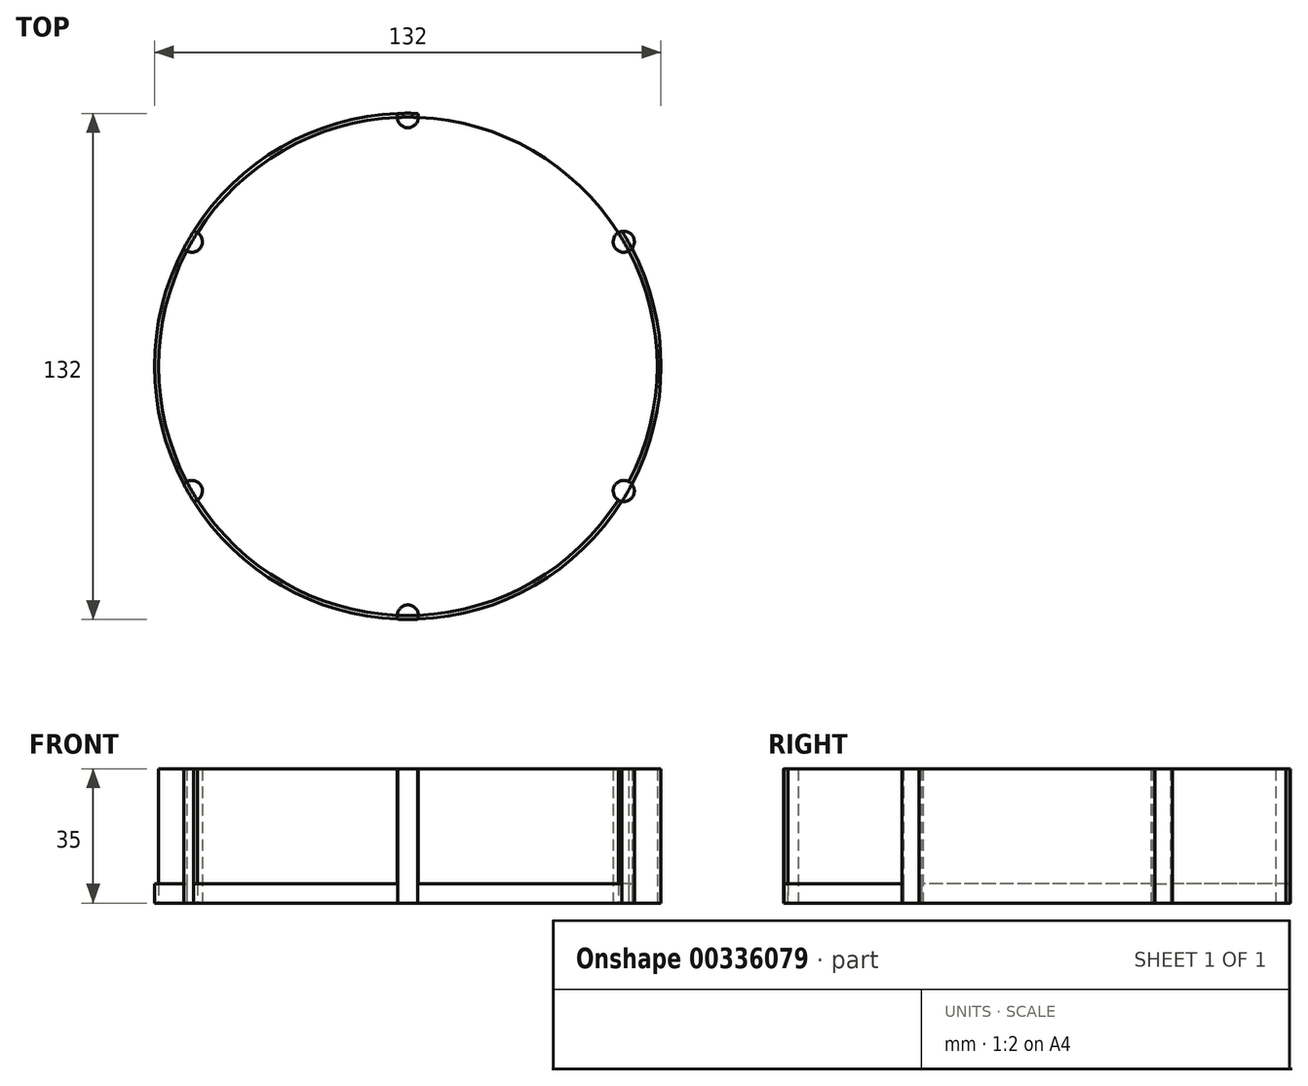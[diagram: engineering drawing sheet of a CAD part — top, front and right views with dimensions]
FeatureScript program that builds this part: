
annotation { "Feature Type Name" : "Feature", "Feature Type Description" : "" }
export const myFeature = defineFeature(function(context is Context, id is Id, definition is map)
    precondition{}
    {
        {
            var Q0;
            Q0=qCreatedBy(makeId("Top.planeOp"),FACE);
            var sketch = newSketch(context, id + "F0", { "sketchPlane" : qUnion([Q0])});
            skCircle(sketch, "E0", {"center": v(0, 0) * mm, "radius": 65 * mm});
            skCircle(sketch, "E1", {"center": v(0, 65) * mm, "radius": 2.75 * mm});
            skCircle(sketch, "E2.1.0", {"center": v(-56.3, 32.5) * mm, "radius": 2.75 * mm});
            skCircle(sketch, "E2.2.0", {"center": v(-56.3, -32.5) * mm, "radius": 2.75 * mm});
            skCircle(sketch, "E2.3.0", {"center": v(0, -65) * mm, "radius": 2.75 * mm});
            skCircle(sketch, "E2.4.0", {"center": v(56.3, -32.5) * mm, "radius": 2.75 * mm});
            skCircle(sketch, "E2.5.0", {"center": v(56.3, 32.5) * mm, "radius": 2.75 * mm});
            skCircle(sketch, "E3.0", {"center": v(0, 0) * mm, "radius": 66 * mm});
            skSolve(sketch);
        }
        {
            var Q0;
            {var subQ0=sQuery(id+"F0.wireOp",EDGE,"E2.2.0");var subQ1=sQuery(id+"F0.wireOp",EDGE,"E0");var subQ2=makeQuery(id+"F0.imprint","INTERSECT",VERTEX,{"disambiguationData":[OD(0.0)],"derivedFrom":[subQ1,subQ0]});Q0=makeQuery(id+"F0.imprint","IMPRINT",FACE,{"disambiguationData":[TD([[makeQuery(id+"F0.imprint","IMPRINT",EDGE,{"disambiguationData":[TD([[subQ2,-1.0]])],"derivedFrom":subQ1}),1.0]])]});}
            var Q1;
            {var subQ0=sQuery(id+"F0.wireOp",EDGE,"E2.2.0");var subQ1=sQuery(id+"F0.wireOp",EDGE,"E0");var subQ2=makeQuery(id+"F0.imprint","INTERSECT",VERTEX,{"disambiguationData":[OD(0.0)],"derivedFrom":[subQ1,subQ0]});Q1=makeQuery(id+"F0.imprint","IMPRINT",FACE,{"disambiguationData":[TD([[makeQuery(id+"F0.imprint","IMPRINT",EDGE,{"disambiguationData":[TD([[subQ2,-1.0]])],"derivedFrom":subQ1}),-1.0]])]});}
            var Q2;
            {var subQ0=sQuery(id+"F0.wireOp",EDGE,"E3.0");var subQ1=sQuery(id+"F0.wireOp",EDGE,"E2.2.0");var subQ2=makeQuery(id+"F0.imprint","INTERSECT",VERTEX,{"disambiguationData":[OD(0.0)],"derivedFrom":[subQ1,subQ0]});Q2=makeQuery(id+"F0.imprint","IMPRINT",FACE,{"disambiguationData":[TD([[makeQuery(id+"F0.imprint","IMPRINT",EDGE,{"disambiguationData":[TD([[subQ2,1.0]])],"derivedFrom":subQ1}),1.0]])]});}
            var Q3;
            {var subQ0=sQuery(id+"F0.wireOp",EDGE,"E2.1.0");var subQ1=sQuery(id+"F0.wireOp",EDGE,"E0");var subQ2=makeQuery(id+"F0.imprint","INTERSECT",VERTEX,{"disambiguationData":[OD(0.0)],"derivedFrom":[subQ1,subQ0]});Q3=makeQuery(id+"F0.imprint","IMPRINT",FACE,{"disambiguationData":[TD([[makeQuery(id+"F0.imprint","IMPRINT",EDGE,{"disambiguationData":[TD([[subQ2,-1.0]])],"derivedFrom":subQ1}),1.0]])]});}
            var Q4;
            {var subQ0=sQuery(id+"F0.wireOp",EDGE,"E2.1.0");var subQ1=sQuery(id+"F0.wireOp",EDGE,"E0");var subQ2=makeQuery(id+"F0.imprint","INTERSECT",VERTEX,{"disambiguationData":[OD(0.0)],"derivedFrom":[subQ1,subQ0]});Q4=makeQuery(id+"F0.imprint","IMPRINT",FACE,{"disambiguationData":[TD([[makeQuery(id+"F0.imprint","IMPRINT",EDGE,{"disambiguationData":[TD([[subQ2,-1.0]])],"derivedFrom":subQ1}),-1.0]])]});}
            var Q5;
            {var subQ0=sQuery(id+"F0.wireOp",EDGE,"E3.0");var subQ1=sQuery(id+"F0.wireOp",EDGE,"E2.1.0");var subQ2=makeQuery(id+"F0.imprint","INTERSECT",VERTEX,{"disambiguationData":[OD(0.0)],"derivedFrom":[subQ1,subQ0]});Q5=makeQuery(id+"F0.imprint","IMPRINT",FACE,{"disambiguationData":[TD([[makeQuery(id+"F0.imprint","IMPRINT",EDGE,{"disambiguationData":[TD([[subQ2,1.0]])],"derivedFrom":subQ1}),1.0]])]});}
            var Q6;
            {var subQ0=sQuery(id+"F0.wireOp",EDGE,"E1");var subQ1=sQuery(id+"F0.wireOp",EDGE,"E0");var subQ2=makeQuery(id+"F0.imprint","INTERSECT",VERTEX,{"disambiguationData":[OD(0.0)],"derivedFrom":[subQ1,subQ0]});Q6=makeQuery(id+"F0.imprint","IMPRINT",FACE,{"disambiguationData":[TD([[makeQuery(id+"F0.imprint","IMPRINT",EDGE,{"disambiguationData":[TD([[subQ2,-1.0]])],"derivedFrom":subQ1}),1.0]])]});}
            var Q7;
            {var subQ0=sQuery(id+"F0.wireOp",EDGE,"E1");var subQ1=sQuery(id+"F0.wireOp",EDGE,"E0");var subQ2=makeQuery(id+"F0.imprint","INTERSECT",VERTEX,{"disambiguationData":[OD(0.0)],"derivedFrom":[subQ1,subQ0]});Q7=makeQuery(id+"F0.imprint","IMPRINT",FACE,{"disambiguationData":[TD([[makeQuery(id+"F0.imprint","IMPRINT",EDGE,{"disambiguationData":[TD([[subQ2,-1.0]])],"derivedFrom":subQ1}),-1.0]])]});}
            var Q8;
            {var subQ0=sQuery(id+"F0.wireOp",EDGE,"E3.0");var subQ1=sQuery(id+"F0.wireOp",EDGE,"E1");var subQ2=makeQuery(id+"F0.imprint","INTERSECT",VERTEX,{"disambiguationData":[OD(0.0)],"derivedFrom":[subQ1,subQ0]});Q8=makeQuery(id+"F0.imprint","IMPRINT",FACE,{"disambiguationData":[TD([[makeQuery(id+"F0.imprint","IMPRINT",EDGE,{"disambiguationData":[TD([[subQ2,1.0]])],"derivedFrom":subQ1}),1.0]])]});}
            var Q9;
            {var subQ0=sQuery(id+"F0.wireOp",EDGE,"E2.5.0");var subQ1=sQuery(id+"F0.wireOp",EDGE,"E0");var subQ2=makeQuery(id+"F0.imprint","INTERSECT",VERTEX,{"disambiguationData":[OD(0.0)],"derivedFrom":[subQ1,subQ0]});Q9=makeQuery(id+"F0.imprint","IMPRINT",FACE,{"disambiguationData":[TD([[makeQuery(id+"F0.imprint","IMPRINT",EDGE,{"disambiguationData":[TD([[subQ2,1.0]])],"derivedFrom":subQ1}),1.0]])]});}
            var Q10;
            {var subQ0=sQuery(id+"F0.wireOp",EDGE,"E2.5.0");var subQ1=sQuery(id+"F0.wireOp",EDGE,"E0");var subQ2=makeQuery(id+"F0.imprint","INTERSECT",VERTEX,{"disambiguationData":[OD(0.0)],"derivedFrom":[subQ1,subQ0]});Q10=makeQuery(id+"F0.imprint","IMPRINT",FACE,{"disambiguationData":[TD([[makeQuery(id+"F0.imprint","IMPRINT",EDGE,{"disambiguationData":[TD([[subQ2,1.0]])],"derivedFrom":subQ1}),-1.0]])]});}
            var Q11;
            {var subQ0=sQuery(id+"F0.wireOp",EDGE,"E3.0");var subQ1=sQuery(id+"F0.wireOp",EDGE,"E2.5.0");var subQ2=makeQuery(id+"F0.imprint","INTERSECT",VERTEX,{"disambiguationData":[OD(0.0)],"derivedFrom":[subQ1,subQ0]});Q11=makeQuery(id+"F0.imprint","IMPRINT",FACE,{"disambiguationData":[TD([[makeQuery(id+"F0.imprint","IMPRINT",EDGE,{"disambiguationData":[TD([[subQ2,1.0]])],"derivedFrom":subQ1}),1.0]])]});}
            var Q12;
            {var subQ0=sQuery(id+"F0.wireOp",EDGE,"E2.4.0");var subQ1=sQuery(id+"F0.wireOp",EDGE,"E0");var subQ2=makeQuery(id+"F0.imprint","INTERSECT",VERTEX,{"disambiguationData":[OD(0.0)],"derivedFrom":[subQ1,subQ0]});Q12=makeQuery(id+"F0.imprint","IMPRINT",FACE,{"disambiguationData":[TD([[makeQuery(id+"F0.imprint","IMPRINT",EDGE,{"disambiguationData":[TD([[subQ2,-1.0]])],"derivedFrom":subQ1}),1.0]])]});}
            var Q13;
            {var subQ0=sQuery(id+"F0.wireOp",EDGE,"E2.4.0");var subQ1=sQuery(id+"F0.wireOp",EDGE,"E0");var subQ2=makeQuery(id+"F0.imprint","INTERSECT",VERTEX,{"disambiguationData":[OD(0.0)],"derivedFrom":[subQ1,subQ0]});Q13=makeQuery(id+"F0.imprint","IMPRINT",FACE,{"disambiguationData":[TD([[makeQuery(id+"F0.imprint","IMPRINT",EDGE,{"disambiguationData":[TD([[subQ2,-1.0]])],"derivedFrom":subQ1}),-1.0]])]});}
            var Q14;
            {var subQ0=sQuery(id+"F0.wireOp",EDGE,"E3.0");var subQ1=sQuery(id+"F0.wireOp",EDGE,"E2.4.0");var subQ2=makeQuery(id+"F0.imprint","INTERSECT",VERTEX,{"disambiguationData":[OD(0.0)],"derivedFrom":[subQ1,subQ0]});Q14=makeQuery(id+"F0.imprint","IMPRINT",FACE,{"disambiguationData":[TD([[makeQuery(id+"F0.imprint","IMPRINT",EDGE,{"disambiguationData":[TD([[subQ2,1.0]])],"derivedFrom":subQ1}),1.0]])]});}
            var Q15;
            {var subQ0=sQuery(id+"F0.wireOp",EDGE,"E2.3.0");var subQ1=sQuery(id+"F0.wireOp",EDGE,"E0");var subQ2=makeQuery(id+"F0.imprint","INTERSECT",VERTEX,{"disambiguationData":[OD(0.0)],"derivedFrom":[subQ1,subQ0]});Q15=makeQuery(id+"F0.imprint","IMPRINT",FACE,{"disambiguationData":[TD([[makeQuery(id+"F0.imprint","IMPRINT",EDGE,{"disambiguationData":[TD([[subQ2,-1.0]])],"derivedFrom":subQ1}),1.0]])]});}
            var Q16;
            {var subQ0=sQuery(id+"F0.wireOp",EDGE,"E2.3.0");var subQ1=sQuery(id+"F0.wireOp",EDGE,"E0");var subQ2=makeQuery(id+"F0.imprint","INTERSECT",VERTEX,{"disambiguationData":[OD(0.0)],"derivedFrom":[subQ1,subQ0]});Q16=makeQuery(id+"F0.imprint","IMPRINT",FACE,{"disambiguationData":[TD([[makeQuery(id+"F0.imprint","IMPRINT",EDGE,{"disambiguationData":[TD([[subQ2,-1.0]])],"derivedFrom":subQ1}),-1.0]])]});}
            var Q17;
            {var subQ0=sQuery(id+"F0.wireOp",EDGE,"E3.0");var subQ1=sQuery(id+"F0.wireOp",EDGE,"E2.3.0");var subQ2=makeQuery(id+"F0.imprint","INTERSECT",VERTEX,{"disambiguationData":[OD(0.0)],"derivedFrom":[subQ1,subQ0]});Q17=makeQuery(id+"F0.imprint","IMPRINT",FACE,{"disambiguationData":[TD([[makeQuery(id+"F0.imprint","IMPRINT",EDGE,{"disambiguationData":[TD([[subQ2,1.0]])],"derivedFrom":subQ1}),1.0]])]});}
            extrude(context, id + "F1", {"entities" : qUnion([Q0, Q1, Q2, Q3, Q4, Q5, Q6, Q7, Q8, Q9, Q10, Q11, Q12, Q13, Q14, Q15, Q16, Q17]), "depth" : 35 * mm});
        }
        {
            var Q0;
            {var subQ0=sQuery(id+"F0.wireOp",EDGE,"E2.2.0");var subQ1=sQuery(id+"F0.wireOp",EDGE,"E0");var subQ2=makeQuery(id+"F0.imprint","INTERSECT",VERTEX,{"disambiguationData":[OD(1.0)],"derivedFrom":[subQ1,subQ0]});Q0=makeQuery(id+"F0.imprint","IMPRINT",FACE,{"disambiguationData":[TD([[makeQuery(id+"F0.imprint","IMPRINT",EDGE,{"disambiguationData":[TD([[subQ2,-1.0]])],"derivedFrom":subQ1}),-1.0]])]});}
            var Q1;
            {var subQ0=sQuery(id+"F0.wireOp",EDGE,"E2.1.0");var subQ1=sQuery(id+"F0.wireOp",EDGE,"E0");var subQ2=makeQuery(id+"F0.imprint","INTERSECT",VERTEX,{"disambiguationData":[OD(1.0)],"derivedFrom":[subQ1,subQ0]});Q1=makeQuery(id+"F0.imprint","IMPRINT",FACE,{"disambiguationData":[TD([[makeQuery(id+"F0.imprint","IMPRINT",EDGE,{"disambiguationData":[TD([[subQ2,-1.0]])],"derivedFrom":subQ1}),-1.0]])]});}
            var Q2;
            {var subQ0=sQuery(id+"F0.wireOp",EDGE,"E1");var subQ1=sQuery(id+"F0.wireOp",EDGE,"E0");var subQ2=makeQuery(id+"F0.imprint","INTERSECT",VERTEX,{"disambiguationData":[OD(1.0)],"derivedFrom":[subQ1,subQ0]});Q2=makeQuery(id+"F0.imprint","IMPRINT",FACE,{"disambiguationData":[TD([[makeQuery(id+"F0.imprint","IMPRINT",EDGE,{"disambiguationData":[TD([[subQ2,-1.0]])],"derivedFrom":subQ1}),-1.0]])]});}
            var Q3;
            {var subQ0=sQuery(id+"F0.wireOp",EDGE,"E2.5.0");var subQ1=sQuery(id+"F0.wireOp",EDGE,"E0");var subQ2=makeQuery(id+"F0.imprint","INTERSECT",VERTEX,{"disambiguationData":[OD(0.0)],"derivedFrom":[subQ1,subQ0]});Q3=makeQuery(id+"F0.imprint","IMPRINT",FACE,{"disambiguationData":[TD([[makeQuery(id+"F0.imprint","IMPRINT",EDGE,{"disambiguationData":[TD([[subQ2,-1.0]])],"derivedFrom":subQ1}),-1.0]])]});}
            var Q4;
            {var subQ0=sQuery(id+"F0.wireOp",EDGE,"E2.5.0");var subQ1=sQuery(id+"F0.wireOp",EDGE,"E0");var subQ2=makeQuery(id+"F0.imprint","INTERSECT",VERTEX,{"disambiguationData":[OD(1.0)],"derivedFrom":[subQ1,subQ0]});Q4=makeQuery(id+"F0.imprint","IMPRINT",FACE,{"disambiguationData":[TD([[makeQuery(id+"F0.imprint","IMPRINT",EDGE,{"disambiguationData":[TD([[subQ2,1.0]])],"derivedFrom":subQ1}),-1.0]])]});}
            var Q5;
            {var subQ0=sQuery(id+"F0.wireOp",EDGE,"E2.3.0");var subQ1=sQuery(id+"F0.wireOp",EDGE,"E0");var subQ2=makeQuery(id+"F0.imprint","INTERSECT",VERTEX,{"disambiguationData":[OD(1.0)],"derivedFrom":[subQ1,subQ0]});Q5=makeQuery(id+"F0.imprint","IMPRINT",FACE,{"disambiguationData":[TD([[makeQuery(id+"F0.imprint","IMPRINT",EDGE,{"disambiguationData":[TD([[subQ2,-1.0]])],"derivedFrom":subQ1}),-1.0]])]});}
            extrude(context, id + "F2", {"entities" : qUnion([Q0, Q1, Q2, Q3, Q4, Q5]), "depth" : 5 * mm});
        }
    });
